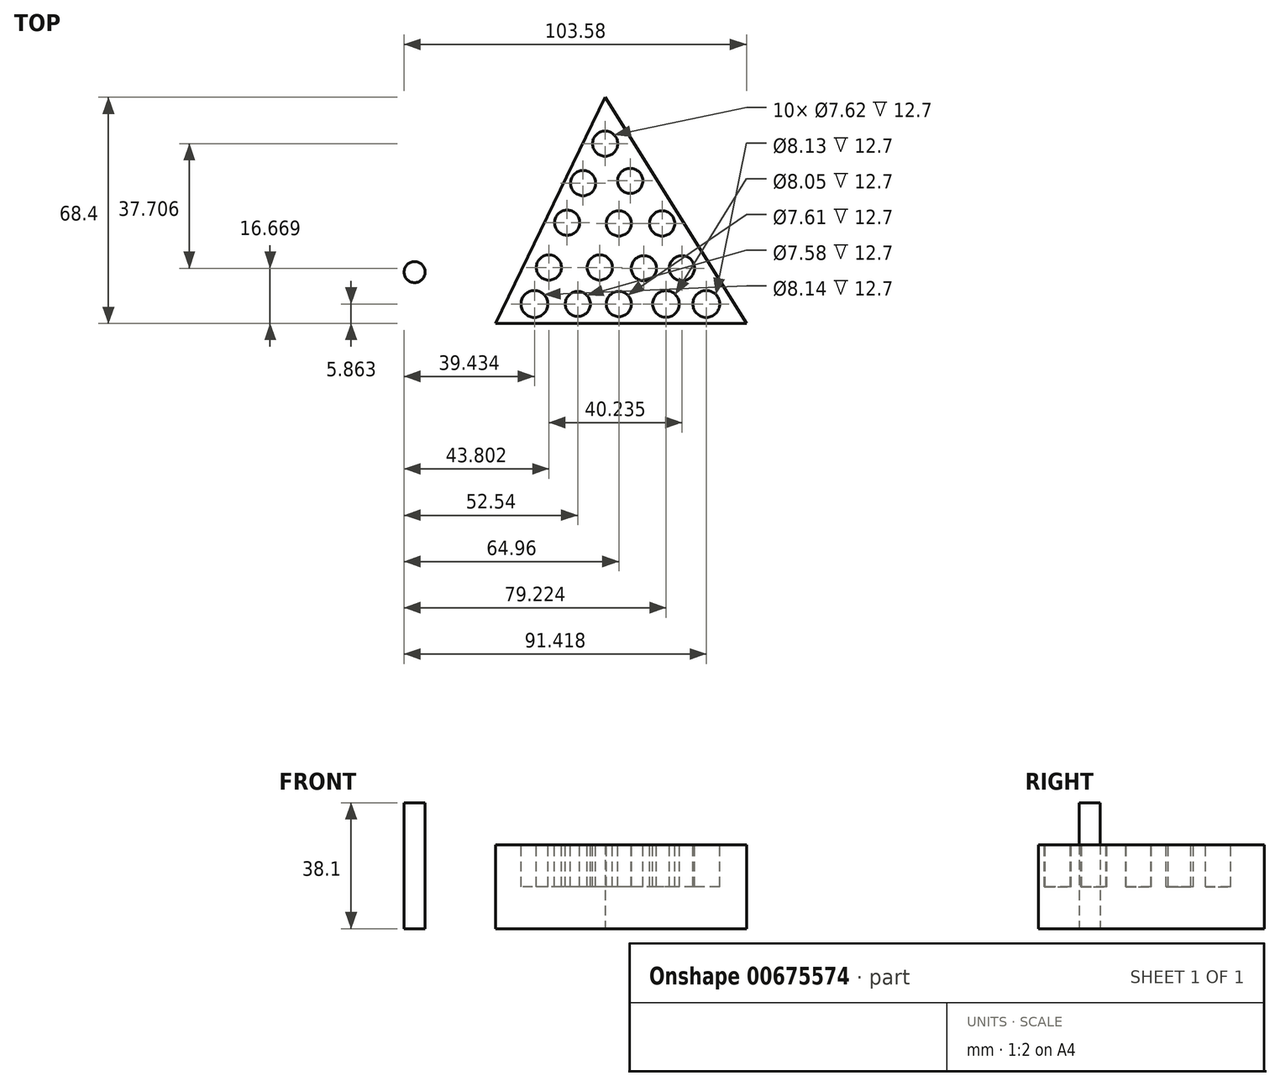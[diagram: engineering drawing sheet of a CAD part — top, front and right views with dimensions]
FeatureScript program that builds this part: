
annotation { "Feature Type Name" : "Feature", "Feature Type Description" : "" }
export const myFeature = defineFeature(function(context is Context, id is Id, definition is map)
    precondition{}
    {
        {
            var Q0;
            Q0=qCreatedBy(makeId("Top.planeOp"),FACE);
            var sketch = newSketch(context, id + "F0", { "sketchPlane" : qUnion([Q0])});
            skLineSegment(sketch, "E0", {"start": v(-75.87, 0) * mm, "end": v(-42.76, 68.4) * mm});
            skLineSegment(sketch, "E1", {"start": v(-42.76, 68.4) * mm, "end": v(0, 0) * mm});
            skLineSegment(sketch, "E2", {"start": v(0, 0) * mm, "end": v(-75.87, 0) * mm});
            skSolve(sketch);
        }
        {
            var Q0;
            Q0 = qSketchRegion(id + "F0", true);
            extrude(context, id + "F1", {"entities" : qUnion([Q0]), "depth" : 25.4 * mm, "offsetDistance" : 25.4 * mm});
        }
        {
            var Q0;
            Q0=makeQuery(id+"F1.opExtrude","CAP_FACE",FACE,{"disambiguationData":[OSD([sQuery(id+"F0.wireOp",EDGE,"E0"),sQuery(id+"F0.wireOp",EDGE,"E1"),sQuery(id+"F0.wireOp",EDGE,"E2")])],"isStart":false});
            var sketch = newSketch(context, id + "F2", { "sketchPlane" : qUnion([Q0])});
            skCircle(sketch, "E3", {"center": v(-64.15, 5.86) * mm, "radius": 4.07 * mm});
            skCircle(sketch, "E4", {"center": v(-51.04, 5.86) * mm, "radius": 3.8 * mm});
            skCircle(sketch, "E5", {"center": v(-38.62, 5.86) * mm, "radius": 3.8 * mm});
            skCircle(sketch, "E6", {"center": v(-24.36, 5.86) * mm, "radius": 4.03 * mm});
            skCircle(sketch, "E7", {"center": v(-12.16, 5.86) * mm, "radius": 4.06 * mm});
            skSolve(sketch);
        }
        {
            var Q0;
            Q0=makeQuery(id+"F2.imprint","IMPRINT",FACE,{"disambiguationData":[TD([[makeQuery(id+"F2.imprint","IMPRINT",EDGE,{"derivedFrom":sQuery(id+"F2.wireOp",EDGE,"E3")}),1.0]])]});
            var Q1;
            Q1=makeQuery(id+"F2.imprint","IMPRINT",FACE,{"disambiguationData":[TD([[makeQuery(id+"F2.imprint","IMPRINT",EDGE,{"derivedFrom":sQuery(id+"F2.wireOp",EDGE,"E4")}),1.0]])]});
            var Q2;
            Q2=makeQuery(id+"F2.imprint","IMPRINT",FACE,{"disambiguationData":[TD([[makeQuery(id+"F2.imprint","IMPRINT",EDGE,{"derivedFrom":sQuery(id+"F2.wireOp",EDGE,"E5")}),1.0]])]});
            var Q3;
            Q3=makeQuery(id+"F2.imprint","IMPRINT",FACE,{"disambiguationData":[TD([[makeQuery(id+"F2.imprint","IMPRINT",EDGE,{"derivedFrom":sQuery(id+"F2.wireOp",EDGE,"E6")}),1.0]])]});
            var Q4;
            Q4=makeQuery(id+"F2.imprint","IMPRINT",FACE,{"disambiguationData":[TD([[makeQuery(id+"F2.imprint","IMPRINT",EDGE,{"derivedFrom":sQuery(id+"F2.wireOp",EDGE,"E7")}),1.0]])]});
            extrude(context, id + "F3", {"entities" : qUnion([Q0, Q1, Q2, Q3, Q4]), "operationType" : NewBodyOperationType.REMOVE, "oppositeDirection" : true, "depth" : 12.7 * mm, "offsetDistance" : 25.4 * mm});
        }
        {
            var Q0;
            Q0=makeQuery(id+"F1.opExtrude","CAP_FACE",FACE,{"disambiguationData":[OSD([sQuery(id+"F0.wireOp",EDGE,"E0"),sQuery(id+"F0.wireOp",EDGE,"E1"),sQuery(id+"F0.wireOp",EDGE,"E2")])],"isStart":false});
            var sketch = newSketch(context, id + "F4", { "sketchPlane" : qUnion([Q0])});
            skCircle(sketch, "E8", {"center": v(-59.78, 16.9) * mm, "radius": 3.81 * mm});
            skCircle(sketch, "E9", {"center": v(-44.37, 16.9) * mm, "radius": 3.81 * mm});
            skCircle(sketch, "E10", {"center": v(-31.04, 16.67) * mm, "radius": 3.81 * mm});
            skCircle(sketch, "E11", {"center": v(-19.54, 16.67) * mm, "radius": 3.81 * mm});
            skSolve(sketch);
        }
        {
            var Q0;
            Q0 = qSketchRegion(id + "F4", true);
            extrude(context, id + "F5", {"entities" : qUnion([Q0]), "operationType" : NewBodyOperationType.REMOVE, "oppositeDirection" : true, "depth" : 12.7 * mm, "offsetDistance" : 25.4 * mm});
        }
        {
            var Q0;
            Q0=makeQuery(id+"F1.opExtrude","CAP_FACE",FACE,{"disambiguationData":[OSD([sQuery(id+"F0.wireOp",EDGE,"E0"),sQuery(id+"F0.wireOp",EDGE,"E1"),sQuery(id+"F0.wireOp",EDGE,"E2")])],"isStart":false});
            var sketch = newSketch(context, id + "F6", { "sketchPlane" : qUnion([Q0])});
            skCircle(sketch, "E12", {"center": v(-54.26, 30.46) * mm, "radius": 3.81 * mm});
            skCircle(sketch, "E13", {"center": v(-38.63, 30.23) * mm, "radius": 3.81 * mm});
            skCircle(sketch, "E14", {"center": v(-25.52, 30.23) * mm, "radius": 3.81 * mm});
            skCircle(sketch, "E15", {"center": v(-49.43, 42.42) * mm, "radius": 3.81 * mm});
            skCircle(sketch, "E16", {"center": v(-35.18, 43.1) * mm, "radius": 3.81 * mm});
            skCircle(sketch, "E17", {"center": v(-42.76, 54.37) * mm, "radius": 3.81 * mm});
            skSolve(sketch);
        }
        {
            var Q0;
            Q0 = qSketchRegion(id + "F6", true);
            extrude(context, id + "F7", {"entities" : qUnion([Q0]), "operationType" : NewBodyOperationType.REMOVE, "oppositeDirection" : true, "depth" : 12.7 * mm, "offsetDistance" : 25.4 * mm});
        }
        {
            var Q0;
            Q0=qCreatedBy(makeId("Top.planeOp"),FACE);
            var sketch = newSketch(context, id + "F8", { "sketchPlane" : qUnion([Q0])});
            skCircle(sketch, "E18", {"center": v(-100.4, 15.52) * mm, "radius": 3.18 * mm});
            skSolve(sketch);
        }
        {
            var Q0;
            Q0 = qSketchRegion(id + "F8", true);
            extrude(context, id + "F9", {"entities" : qUnion([Q0]), "depth" : 38.1 * mm, "offsetDistance" : 25.4 * mm});
        }
    });
